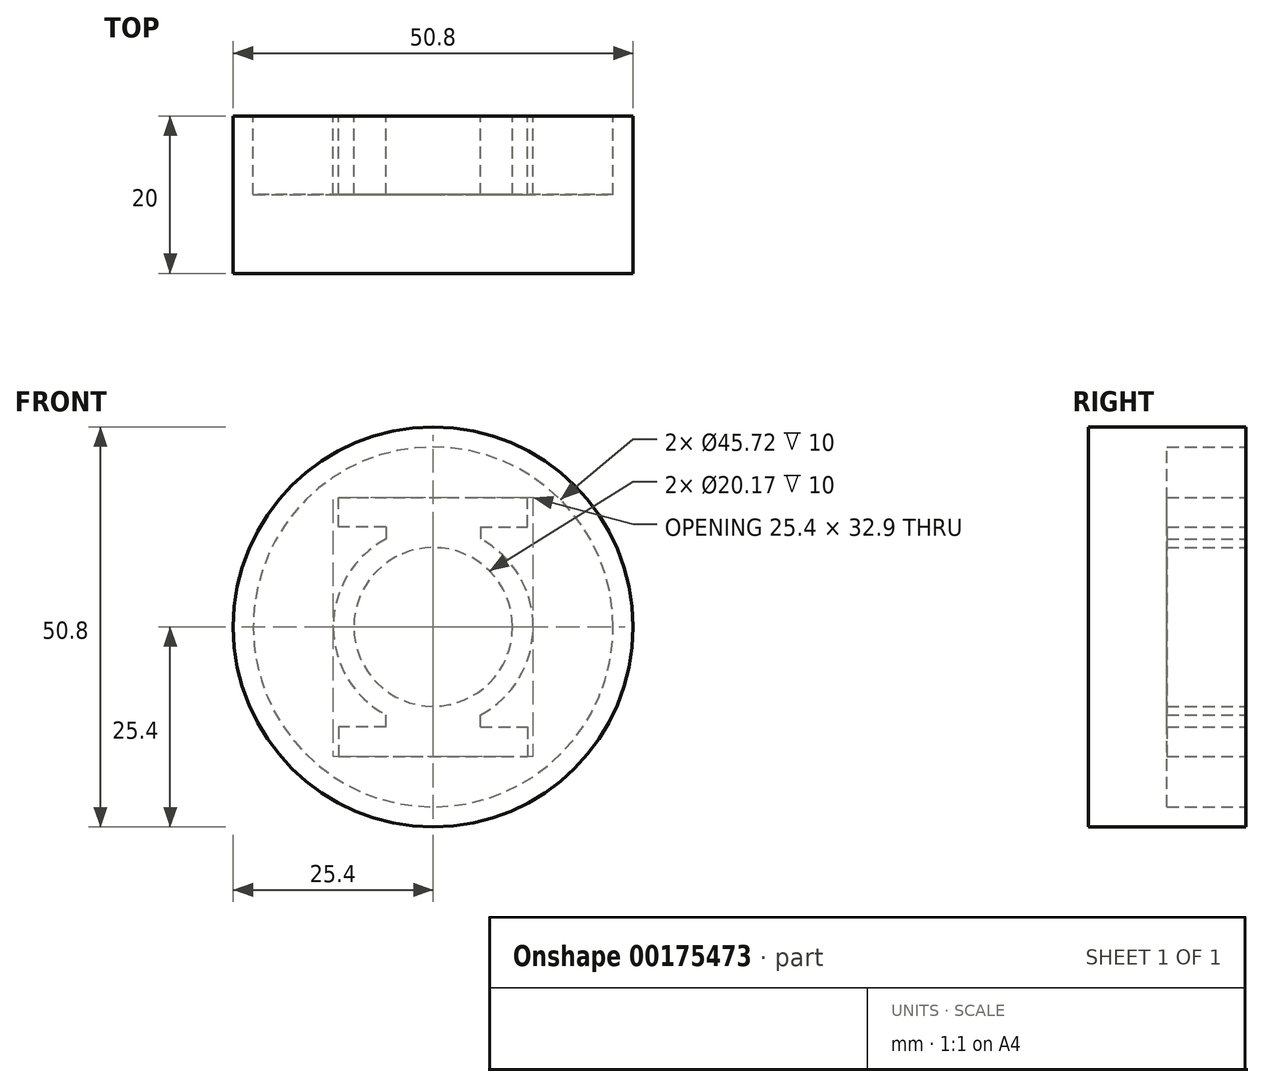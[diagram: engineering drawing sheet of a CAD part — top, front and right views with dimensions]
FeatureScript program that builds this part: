
annotation { "Feature Type Name" : "Feature", "Feature Type Description" : "" }
export const myFeature = defineFeature(function(context is Context, id is Id, definition is map)
    precondition{}
    {
        {
            var Q0;
            Q0=qCreatedBy(makeId("Front.planeOp"),FACE);
            var sketch = newSketch(context, id + "F0", { "sketchPlane" : qUnion([Q0])});
            skCircle(sketch, "E0", {"center": v(0, 0) * mm, "radius": 12.7 * mm});
            skCircle(sketch, "E1", {"center": v(0, 0) * mm, "radius": 22.86 * mm});
            skCircle(sketch, "E2", {"center": v(0, 0) * mm, "radius": 25.4 * mm});
            skCircle(sketch, "E3", {"center": v(0, 0) * mm, "radius": 10.08 * mm});
            skLineSegment(sketch, "E4", {"start": v(0, 0) * mm, "end": v(0, 10.08) * mm});
            skLineSegment(sketch, "E5", {"start": v(0, 0) * mm, "end": v(0, -10.08) * mm});
            skLineSegment(sketch, "E6", {"start": v(0, 10.08) * mm, "end": v(0, 12.7) * mm});
            skLineSegment(sketch, "E7", {"start": v(0, -10.08) * mm, "end": v(0, -12.7) * mm});
            skLineSegment(sketch, "E8", {"start": v(0, -12.7) * mm, "end": v(12, -12.7) * mm});
            skLineSegment(sketch, "E9", {"start": v(0, -12.7) * mm, "end": v(-12, -12.7) * mm});
            skLineSegment(sketch, "E10", {"start": v(0, 12.7) * mm, "end": v(-12, 12.7) * mm});
            skLineSegment(sketch, "E11", {"start": v(0, 12.7) * mm, "end": v(12, 12.7) * mm});
            skLineSegment(sketch, "E12", {"start": v(-12, 12.7) * mm, "end": v(-12, 16.45) * mm});
            skLineSegment(sketch, "E13", {"start": v(-12, 16.45) * mm, "end": v(12, 16.45) * mm});
            skLineSegment(sketch, "E14", {"start": v(12, 12.7) * mm, "end": v(12, 16.45) * mm});
            skLineSegment(sketch, "E15", {"start": v(-12, -12.7) * mm, "end": v(-12, -16.45) * mm});
            skLineSegment(sketch, "E16", {"start": v(-12, -16.45) * mm, "end": v(12, -16.45) * mm});
            skLineSegment(sketch, "E17", {"start": v(12, -12.7) * mm, "end": v(12, -16.45) * mm});
            skLineSegment(sketch, "E18", {"start": v(-6, -12.7) * mm, "end": v(-6, -11.2) * mm});
            skLineSegment(sketch, "E19", {"start": v(6, -12.7) * mm, "end": v(6, -11.2) * mm});
            skLineSegment(sketch, "E20", {"start": v(6, 12.7) * mm, "end": v(6, 11.2) * mm});
            skLineSegment(sketch, "E21", {"start": v(-6, 12.7) * mm, "end": v(-6, 11.2) * mm});
            skSolve(sketch);
        }
        {
            var Q0;
            {var subQ0=sQuery(id+"F0.wireOp",EDGE,"E15");Q0=makeQuery(id+"F0.imprint","IMPRINT",FACE,{"disambiguationData":[TD([[makeQuery(id+"F0.imprint","IMPRINT",EDGE,{"derivedFrom":subQ0}),1.0]])]});}
            var Q1;
            {var subQ0=sQuery(id+"F0.wireOp",EDGE,"E6");Q1=makeQuery(id+"F0.imprint","IMPRINT",FACE,{"disambiguationData":[TD([[makeQuery(id+"F0.imprint","IMPRINT",EDGE,{"derivedFrom":subQ0}),1.0]])]});}
            var Q2;
            {var subQ5=sQuery(id+"F0.wireOp",EDGE,"E12");Q2=makeQuery(id+"F0.imprint","IMPRINT",FACE,{"disambiguationData":[TD([[makeQuery(id+"F0.imprint","IMPRINT",EDGE,{"derivedFrom":subQ5}),-1.0]])]});}
            var Q3;
            {var subQ0=sQuery(id+"F0.wireOp",EDGE,"E4");Q3=makeQuery(id+"F0.imprint","IMPRINT",FACE,{"disambiguationData":[TD([[makeQuery(id+"F0.imprint","IMPRINT",EDGE,{"derivedFrom":subQ0}),1.0]])]});}
            var Q4;
            Q4=makeQuery(id+"F0.imprint","IMPRINT",FACE,{"disambiguationData":[TD([[makeQuery(id+"F0.imprint","IMPRINT",EDGE,{"derivedFrom":sQuery(id+"F0.wireOp",EDGE,"E1")}),1.0]])]});
            var Q5;
            {var subQ0=sQuery(id+"F0.wireOp",EDGE,"E6");Q5=makeQuery(id+"F0.imprint","IMPRINT",FACE,{"disambiguationData":[TD([[makeQuery(id+"F0.imprint","IMPRINT",EDGE,{"derivedFrom":subQ0}),-1.0]])]});}
            var Q6;
            {var subQ0=sQuery(id+"F0.wireOp",EDGE,"E4");Q6=makeQuery(id+"F0.imprint","IMPRINT",FACE,{"disambiguationData":[TD([[makeQuery(id+"F0.imprint","IMPRINT",EDGE,{"derivedFrom":subQ0}),-1.0]])]});}
            var Q7;
            Q7=makeQuery(id+"F0.imprint","IMPRINT",FACE,{"disambiguationData":[TD([[makeQuery(id+"F0.imprint","IMPRINT",EDGE,{"derivedFrom":sQuery(id+"F0.wireOp",EDGE,"E1")}),-1.0]])]});
            var Q8;
            {var subQ3=sQuery(id+"F0.wireOp",EDGE,"E19");Q8=makeQuery(id+"F0.imprint","IMPRINT",FACE,{"disambiguationData":[TD([[makeQuery(id+"F0.imprint","IMPRINT",EDGE,{"derivedFrom":subQ3}),1.0]])]});}
            var Q9;
            {var subQ3=sQuery(id+"F0.wireOp",EDGE,"E20");Q9=makeQuery(id+"F0.imprint","IMPRINT",FACE,{"disambiguationData":[TD([[makeQuery(id+"F0.imprint","IMPRINT",EDGE,{"derivedFrom":subQ3}),-1.0]])]});}
            var Q10;
            {var subQ3=sQuery(id+"F0.wireOp",EDGE,"E18");Q10=makeQuery(id+"F0.imprint","IMPRINT",FACE,{"disambiguationData":[TD([[makeQuery(id+"F0.imprint","IMPRINT",EDGE,{"derivedFrom":subQ3}),-1.0]])]});}
            var Q11;
            {var subQ3=sQuery(id+"F0.wireOp",EDGE,"E21");Q11=makeQuery(id+"F0.imprint","IMPRINT",FACE,{"disambiguationData":[TD([[makeQuery(id+"F0.imprint","IMPRINT",EDGE,{"derivedFrom":subQ3}),1.0]])]});}
            extrude(context, id + "F1", {"entities" : qUnion([Q0, Q1, Q2, Q3, Q4, Q5, Q6, Q7, Q8, Q9, Q10, Q11]), "depth" : 20 * mm});
        }
        {
            var Q0;
            {var subQ0=sQuery(id+"F0.wireOp",EDGE,"E4");Q0=makeQuery(id+"F0.imprint","IMPRINT",FACE,{"disambiguationData":[TD([[makeQuery(id+"F0.imprint","IMPRINT",EDGE,{"derivedFrom":subQ0}),1.0]])]});}
            var Q1;
            {var subQ0=sQuery(id+"F0.wireOp",EDGE,"E4");Q1=makeQuery(id+"F0.imprint","IMPRINT",FACE,{"disambiguationData":[TD([[makeQuery(id+"F0.imprint","IMPRINT",EDGE,{"derivedFrom":subQ0}),-1.0]])]});}
            var Q2;
            Q2=makeQuery(id+"F0.imprint","IMPRINT",FACE,{"disambiguationData":[TD([[makeQuery(id+"F0.imprint","IMPRINT",EDGE,{"derivedFrom":sQuery(id+"F0.wireOp",EDGE,"E1")}),1.0]])]});
            extrude(context, id + "F2", {"entities" : qUnion([Q0, Q1, Q2]), "operationType" : NewBodyOperationType.REMOVE, "depth" : 10 * mm});
        }
    });
